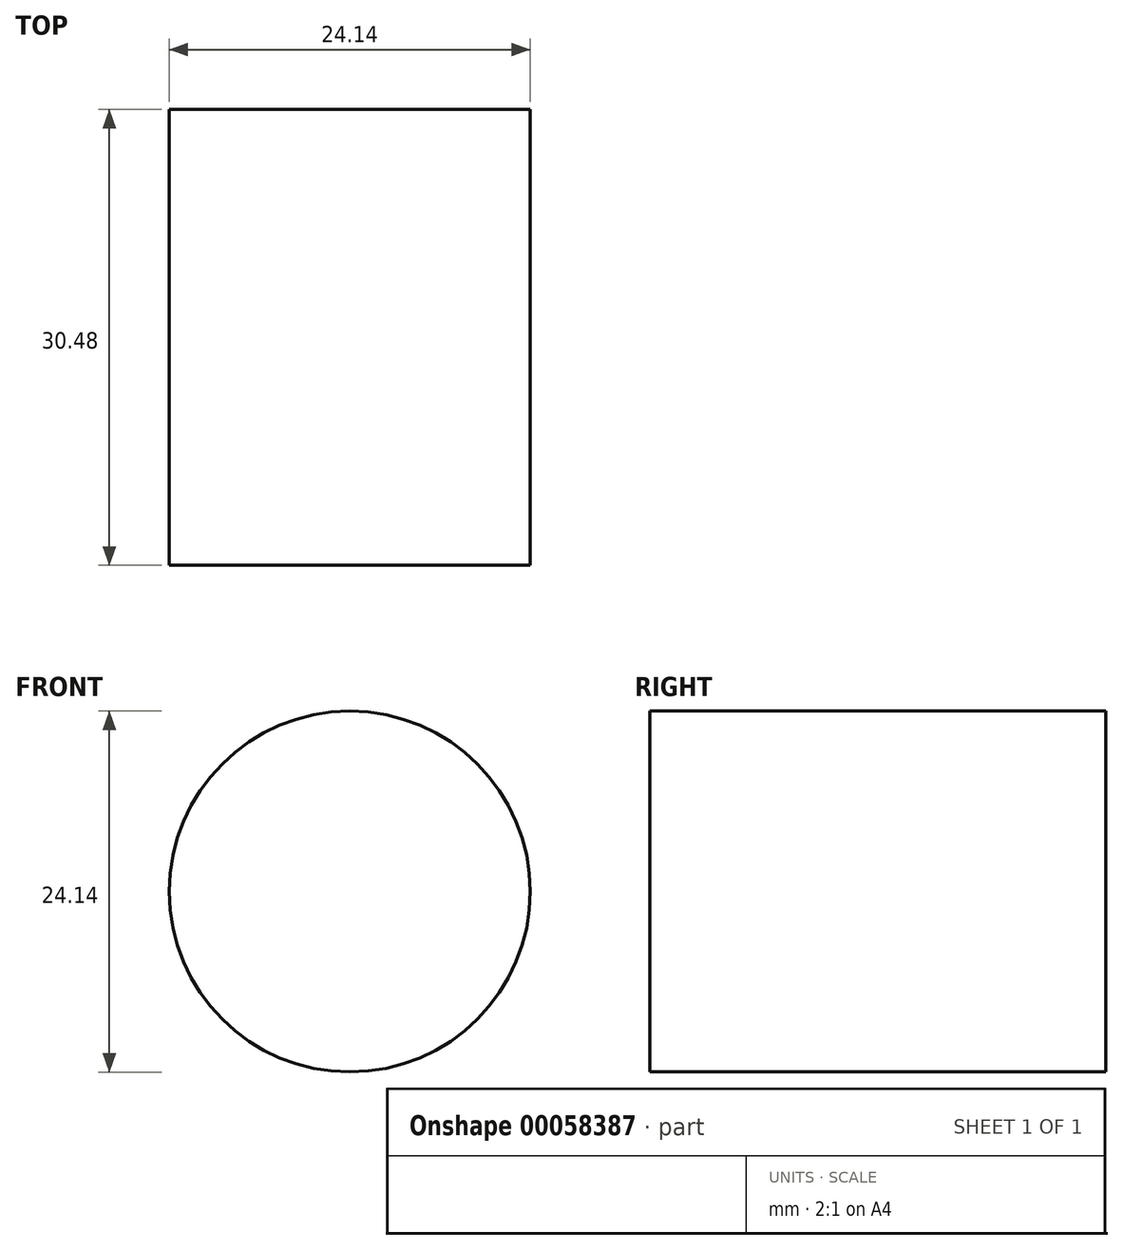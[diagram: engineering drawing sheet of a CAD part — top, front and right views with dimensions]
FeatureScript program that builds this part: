
annotation { "Feature Type Name" : "Feature", "Feature Type Description" : "" }
export const myFeature = defineFeature(function(context is Context, id is Id, definition is map)
    precondition{}
    {
        {
            var Q0;
            Q0=qCreatedBy(makeId("Front.planeOp"),FACE);
            var sketch = newSketch(context, id + "F0", { "sketchPlane" : qUnion([Q0])});
            skCircle(sketch, "E0", {"center": v(0, 0) * mm, "radius": 12.07 * mm});
            skSolve(sketch);
        }
        {
            var Q0;
            Q0=makeQuery(id+"F0.imprint","IMPRINT",FACE,{"disambiguationData":[TD([[makeQuery(id+"F0.imprint","IMPRINT",EDGE,{"derivedFrom":sQuery(id+"F0.wireOp",EDGE,"E0")}),1.0]])]});
            extrude(context, id + "F1", {"entities" : qUnion([Q0]), "depth" : 30.48 * mm});
        }
    });
